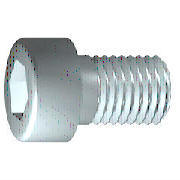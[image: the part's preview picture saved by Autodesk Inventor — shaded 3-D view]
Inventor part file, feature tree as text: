
AUTODESK INVENTOR PART (.ipt)
format: ipt  version: 2022 (Build 260153000, 153)  size: 189,952 bytes
history: native  units: mm (DEFAULTED — no unit token found)
features: sketch x2, extrude x1, plane x1, fillet x1
ambient origin geometry x7: Origin, YZ Plane, XY Plane, X Axis, Y Axis, Z Axis, Center Point
bodies: Solid1 (feature_tree), Body (feature_tree)
feature tree (5):
  extrude  "Slot"  Depth=6.0mm
  plane  "Work Plane1"
  fillet  "Fillet2"  Radius=6.0mm
  sketch  "Sketch1"  dims[d1=27.5mm d2=0.61355mm d3=6.0mm]
  sketch  "Sketch2"  dims[d4=3.0mm d5=60.0deg d6=6.0mm d7=6.0mm d8=5.773503mm d9=10.0mm d10=90.0deg d11=10.0mm d12=0.0mm d13=27.5mm d14=0.0mm d15=0.61345mm d16=0.61345mm d17=0.6mm d19=0.0mm d26=30.0mm d27=45.0deg d28=0.0mm d29=0.0mm d30=0.1mm]
